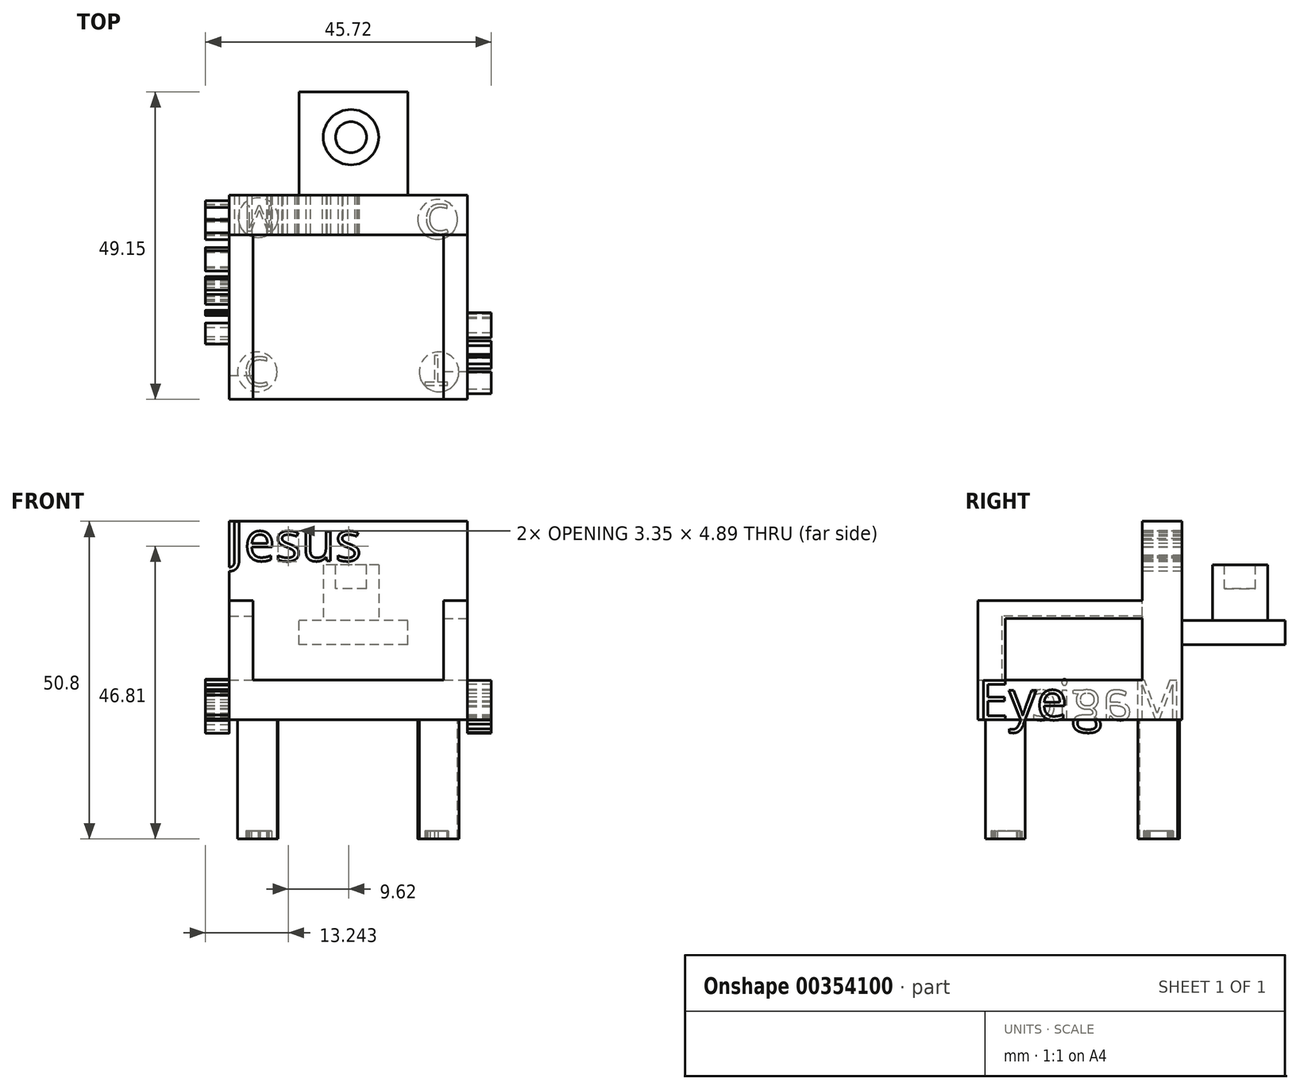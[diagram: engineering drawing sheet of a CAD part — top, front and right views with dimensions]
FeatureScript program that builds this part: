
annotation { "Feature Type Name" : "Feature", "Feature Type Description" : "" }
export const myFeature = defineFeature(function(context is Context, id is Id, definition is map)
    precondition{}
    {
        {
            var Q0;
            Q0=qCreatedBy(makeId("Top.planeOp"),FACE);
            var sketch = newSketch(context, id + "F0", { "sketchPlane" : qUnion([Q0])});
            skLineSegment(sketch, "E0.bottom", {"start": v(-18.82, -4.38) * mm, "end": v(19.28, -4.38) * mm});
            skLineSegment(sketch, "E0.top", {"start": v(-18.82, 28.26) * mm, "end": v(19.28, 28.26) * mm});
            skLineSegment(sketch, "E0.left", {"start": v(-18.82, -4.38) * mm, "end": v(-18.82, 28.26) * mm});
            skLineSegment(sketch, "E0.right", {"start": v(19.28, -4.38) * mm, "end": v(19.28, 28.26) * mm});
            skSolve(sketch);
        }
        {
            var Q0;
            Q0 = qSketchRegion(id + "F0", true);
            extrude(context, id + "F1", {"entities" : qUnion([Q0]), "depth" : 6.35 * mm});
        }
        {
            var Q0;
            Q0=makeQuery(id+"F1.opExtrude","CAP_FACE",FACE,{"disambiguationData":[OSD([sQuery(id+"F0.wireOp",EDGE,"E0.bottom"),sQuery(id+"F0.wireOp",EDGE,"E0.top"),sQuery(id+"F0.wireOp",EDGE,"E0.left"),sQuery(id+"F0.wireOp",EDGE,"E0.right")])],"isStart":false});
            var sketch = newSketch(context, id + "F2", { "sketchPlane" : qUnion([Q0])});
            skLineSegment(sketch, "E1.bottom", {"start": v(-18.82, 21.91) * mm, "end": v(19.28, 21.91) * mm});
            skLineSegment(sketch, "E1.top", {"start": v(-18.82, 28.26) * mm, "end": v(19.28, 28.26) * mm});
            skLineSegment(sketch, "E1.left", {"start": v(-18.82, 21.91) * mm, "end": v(-18.82, 28.26) * mm});
            skLineSegment(sketch, "E1.right", {"start": v(19.28, 21.91) * mm, "end": v(19.28, 28.26) * mm});
            skSolve(sketch);
        }
        {
            var Q0;
            Q0=makeQuery(id+"F2.imprint","IMPRINT",FACE,{"disambiguationData":[TD([[makeQuery(id+"F2.imprint","IMPRINT",EDGE,{"derivedFrom":sQuery(id+"F2.wireOp",EDGE,"E1.bottom")}),1.0]])]});
            extrude(context, id + "F3", {"entities" : qUnion([Q0]), "operationType" : NewBodyOperationType.ADD, "depth" : 25.4 * mm});
        }
        {
            var Q0;
            Q0=makeQuery(id+"F1.opExtrude","CAP_FACE",FACE,{"disambiguationData":[OSD([sQuery(id+"F0.wireOp",EDGE,"E0.bottom"),sQuery(id+"F0.wireOp",EDGE,"E0.top"),sQuery(id+"F0.wireOp",EDGE,"E0.left"),sQuery(id+"F0.wireOp",EDGE,"E0.right")])],"isStart":true});
            var sketch = newSketch(context, id + "F4", { "sketchPlane" : qUnion([Q0])});
            skCircle(sketch, "E2", {"center": v(-14.37, 0) * mm, "radius": 3.18 * mm});
            skSolve(sketch);
        }
        {
            var Q0;
            Q0 = qSketchRegion(id + "F4", true);
            extrude(context, id + "F5", {"entities" : qUnion([Q0]), "operationType" : NewBodyOperationType.ADD, "depth" : 19.05 * mm});
        }
        {
            var Q0;
            Q0=makeQuery(id+"F1.opExtrude","CAP_FACE",FACE,{"disambiguationData":[OSD([sQuery(id+"F0.wireOp",EDGE,"E0.bottom"),sQuery(id+"F0.wireOp",EDGE,"E0.top"),sQuery(id+"F0.wireOp",EDGE,"E0.left"),sQuery(id+"F0.wireOp",EDGE,"E0.right")])],"isStart":true});
            var sketch = newSketch(context, id + "F6", { "sketchPlane" : qUnion([Q0])});
            skCircle(sketch, "E3", {"center": v(14.71, 0) * mm, "radius": 3.18 * mm});
            skSolve(sketch);
        }
        {
            var Q0;
            Q0 = qSketchRegion(id + "F6", true);
            extrude(context, id + "F7", {"entities" : qUnion([Q0]), "operationType" : NewBodyOperationType.ADD, "depth" : 19.05 * mm});
        }
        {
            var Q0;
            Q0=makeQuery(id+"F1.opExtrude","CAP_FACE",FACE,{"disambiguationData":[OSD([sQuery(id+"F0.wireOp",EDGE,"E0.bottom"),sQuery(id+"F0.wireOp",EDGE,"E0.top"),sQuery(id+"F0.wireOp",EDGE,"E0.left"),sQuery(id+"F0.wireOp",EDGE,"E0.right")])],"isStart":true});
            var sketch = newSketch(context, id + "F8", { "sketchPlane" : qUnion([Q0])});
            skCircle(sketch, "E4", {"center": v(-14.23, -24.67) * mm, "radius": 3.18 * mm});
            skSolve(sketch);
        }
        {
            var Q0;
            Q0 = qSketchRegion(id + "F8", true);
            extrude(context, id + "F9", {"entities" : qUnion([Q0]), "operationType" : NewBodyOperationType.ADD, "depth" : 19.05 * mm});
        }
        {
            var Q0;
            Q0=makeQuery(id+"F1.opExtrude","CAP_FACE",FACE,{"disambiguationData":[OSD([sQuery(id+"F0.wireOp",EDGE,"E0.bottom"),sQuery(id+"F0.wireOp",EDGE,"E0.top"),sQuery(id+"F0.wireOp",EDGE,"E0.left"),sQuery(id+"F0.wireOp",EDGE,"E0.right")])],"isStart":true});
            var sketch = newSketch(context, id + "F10", { "sketchPlane" : qUnion([Q0])});
            skCircle(sketch, "E5", {"center": v(14.5, -24.4) * mm, "radius": 3.18 * mm});
            skSolve(sketch);
        }
        {
            var Q0;
            Q0 = qSketchRegion(id + "F10", true);
            extrude(context, id + "F11", {"entities" : qUnion([Q0]), "operationType" : NewBodyOperationType.ADD, "depth" : 19.05 * mm});
        }
        {
            var Q0;
            Q0=makeQuery(id+"F1.opExtrude","CAP_FACE",FACE,{"disambiguationData":[OSD([sQuery(id+"F0.wireOp",EDGE,"E0.bottom"),sQuery(id+"F0.wireOp",EDGE,"E0.top"),sQuery(id+"F0.wireOp",EDGE,"E0.left"),sQuery(id+"F0.wireOp",EDGE,"E0.right")])],"isStart":false});
            var sketch = newSketch(context, id + "F12", { "sketchPlane" : qUnion([Q0])});
            skLineSegment(sketch, "E6.bottom", {"start": v(-18.82, -4.38) * mm, "end": v(-15.01, -4.38) * mm});
            skLineSegment(sketch, "E6.top", {"start": v(-18.82, -0.58) * mm, "end": v(-15.01, -0.58) * mm});
            skLineSegment(sketch, "E6.left", {"start": v(-18.82, -4.38) * mm, "end": v(-18.82, -0.58) * mm});
            skLineSegment(sketch, "E6.right", {"start": v(-15.01, -4.38) * mm, "end": v(-15.01, -0.58) * mm});
            skSolve(sketch);
        }
        {
            var Q0;
            Q0 = qSketchRegion(id + "F12", true);
            extrude(context, id + "F13", {"entities" : qUnion([Q0]), "operationType" : NewBodyOperationType.ADD, "depth" : 12.7 * mm});
        }
        {
            var Q0;
            Q0=makeQuery(id+"F1.opExtrude","CAP_FACE",FACE,{"disambiguationData":[OSD([sQuery(id+"F0.wireOp",EDGE,"E0.bottom"),sQuery(id+"F0.wireOp",EDGE,"E0.top"),sQuery(id+"F0.wireOp",EDGE,"E0.left"),sQuery(id+"F0.wireOp",EDGE,"E0.right")])],"isStart":false});
            var sketch = newSketch(context, id + "F14", { "sketchPlane" : qUnion([Q0])});
            skLineSegment(sketch, "E7.bottom", {"start": v(19.28, -4.38) * mm, "end": v(15.47, -4.38) * mm});
            skLineSegment(sketch, "E7.top", {"start": v(19.28, 0) * mm, "end": v(15.47, 0) * mm});
            skLineSegment(sketch, "E7.left", {"start": v(19.28, -4.38) * mm, "end": v(19.28, 0) * mm});
            skLineSegment(sketch, "E7.right", {"start": v(15.47, -4.38) * mm, "end": v(15.47, 0) * mm});
            skSolve(sketch);
        }
        {
            var Q0;
            Q0 = qSketchRegion(id + "F14", true);
            extrude(context, id + "F15", {"entities" : qUnion([Q0]), "operationType" : NewBodyOperationType.ADD, "depth" : 12.7 * mm});
        }
        {
            var Q0;
            Q0=makeQuery(id+"F13.opExtrude","SWEPT_FACE",FACE,{"disambiguationData":[OSD([sQuery(id+"F12.wireOp",EDGE,"E6.top")])]});
            var sketch = newSketch(context, id + "F16", { "sketchPlane" : qUnion([Q0])});
            skLineSegment(sketch, "E8.bottom", {"start": v(15.01, 16.57) * mm, "end": v(18.82, 16.57) * mm});
            skLineSegment(sketch, "E8.top", {"start": v(15.01, 19.05) * mm, "end": v(18.82, 19.05) * mm});
            skLineSegment(sketch, "E8.left", {"start": v(15.01, 16.57) * mm, "end": v(15.01, 19.05) * mm});
            skLineSegment(sketch, "E8.right", {"start": v(18.82, 16.57) * mm, "end": v(18.82, 19.05) * mm});
            skSolve(sketch);
        }
        {
            var Q0;
            Q0=makeQuery(id+"F16.imprint","IMPRINT",FACE,{"disambiguationData":[TD([[makeQuery(id+"F16.imprint","IMPRINT",EDGE,{"derivedFrom":sQuery(id+"F16.wireOp",EDGE,"E8.bottom")}),1.0]])]});
            extrude(context, id + "F17", {"entities" : qUnion([Q0]), "operationType" : NewBodyOperationType.ADD, "depth" : 25.4 * mm});
        }
        {
            var Q0;
            Q0=makeQuery(id+"F15.opExtrude","SWEPT_FACE",FACE,{"disambiguationData":[OSD([sQuery(id+"F14.wireOp",EDGE,"E7.top")])]});
            var sketch = newSketch(context, id + "F18", { "sketchPlane" : qUnion([Q0])});
            skLineSegment(sketch, "E9.bottom", {"start": v(-19.28, 16.23) * mm, "end": v(-15.47, 16.23) * mm});
            skLineSegment(sketch, "E9.top", {"start": v(-19.28, 19.05) * mm, "end": v(-15.47, 19.05) * mm});
            skLineSegment(sketch, "E9.left", {"start": v(-19.28, 16.23) * mm, "end": v(-19.28, 19.05) * mm});
            skLineSegment(sketch, "E9.right", {"start": v(-15.47, 16.23) * mm, "end": v(-15.47, 19.05) * mm});
            skSolve(sketch);
        }
        {
            var Q0;
            Q0 = qSketchRegion(id + "F18", true);
            extrude(context, id + "F19", {"entities" : qUnion([Q0]), "operationType" : NewBodyOperationType.ADD, "depth" : 25.4 * mm});
        }
        {
            var Q0;
            Q0=makeQuery(id+"F3.opExtrude","SWEPT_FACE",FACE,{"disambiguationData":[OSD([sQuery(id+"F2.wireOp",EDGE,"E1.bottom")])]});
            var sketch = newSketch(context, id + "F20", { "sketchPlane" : qUnion([Q0])});
            skText(sketch, "E10", { "text": "Jesus", "fontName": "OpenSans-Regular.ttf"});
            const initialGuessF20  = {"E10": [-0.01882, 0.0254, 1, 0, 0.00635]};
            skSetInitialGuess(sketch, initialGuessF20);
            skSolve(sketch);
        }
        {
            var Q0;
            Q0 = qSketchRegion(id + "F20", true);
            extrude(context, id + "F21", {"entities" : qUnion([Q0]), "operationType" : NewBodyOperationType.REMOVE, "oppositeDirection" : true, "depth" : 27.28 * mm});
        }
        {
            var Q0;
            {var subQ2=sQuery(id+"F12.wireOp",EDGE,"E6.left");var subQ5=sQuery(id+"F0.wireOp",EDGE,"E0.left");var subQ6=sQuery(id+"F0.wireOp",EDGE,"E0.bottom");Q0=makeQuery(id+"F21.boolean.opBoolean","SPLIT",FACE,{"disambiguationData":[TD([makeQuery(id+"F1.opExtrude","SWEPT_FACE",FACE,{"disambiguationData":[OSD([subQ6])]})])],"derivedFrom":makeQuery(id+"F17.boolean.opBoolean","MERGE",FACE,{"derivedFrom":[makeQuery(id+"F13.boolean.opBoolean","MERGE",FACE,{"derivedFrom":[makeQuery(id+"F3.boolean.opBoolean","MERGE",FACE,{"derivedFrom":[makeQuery(id+"F1.opExtrude","SWEPT_FACE",FACE,{"disambiguationData":[OSD([subQ5])]}),makeQuery(id+"F3.opExtrude","SWEPT_FACE",FACE,{"disambiguationData":[OSD([sQuery(id+"F2.wireOp",EDGE,"E1.left")])]})]}),makeQuery(id+"F13.opExtrude","SWEPT_FACE",FACE,{"disambiguationData":[OSD([subQ2])]})]}),makeQuery(id+"F17.opExtrude","SWEPT_FACE",FACE,{"disambiguationData":[OSD([sQuery(id+"F16.wireOp",EDGE,"E8.right")])]})]})});}
            var sketch = newSketch(context, id + "F22", { "sketchPlane" : qUnion([Q0])});
            skText(sketch, "E11", { "text": "Magic", "fontName": "OpenSans-Regular.ttf"});
            const initialGuessF22  = {"E11": [-0.02826, 0, 1, 0, 0.00635]};
            skSetInitialGuess(sketch, initialGuessF22);
            skSolve(sketch);
        }
        {
            var Q0;
            Q0 = qSketchRegion(id + "F22", true);
            extrude(context, id + "F23", {"entities" : qUnion([Q0]), "operationType" : NewBodyOperationType.ADD, "depth" : 3.8 * mm});
        }
        {
            var Q0;
            Q0=makeQuery(id+"F19.boolean.opBoolean","MERGE",FACE,{"derivedFrom":[makeQuery(id+"F15.boolean.opBoolean","MERGE",FACE,{"derivedFrom":[makeQuery(id+"F3.boolean.opBoolean","MERGE",FACE,{"derivedFrom":[makeQuery(id+"F1.opExtrude","SWEPT_FACE",FACE,{"disambiguationData":[OSD([sQuery(id+"F0.wireOp",EDGE,"E0.right")])]}),makeQuery(id+"F3.opExtrude","SWEPT_FACE",FACE,{"disambiguationData":[OSD([sQuery(id+"F2.wireOp",EDGE,"E1.right")])]})]}),makeQuery(id+"F15.opExtrude","SWEPT_FACE",FACE,{"disambiguationData":[OSD([sQuery(id+"F14.wireOp",EDGE,"E7.left")])]})]}),makeQuery(id+"F19.opExtrude","SWEPT_FACE",FACE,{"disambiguationData":[OSD([sQuery(id+"F18.wireOp",EDGE,"E9.left")])]})]});
            var sketch = newSketch(context, id + "F24", { "sketchPlane" : qUnion([Q0])});
            skText(sketch, "E12", { "text": "Eye", "fontName": "OpenSans-Regular.ttf"});
            const initialGuessF24  = {"E12": [-0.00438, 0, 1, 0, 0.00635]};
            skSetInitialGuess(sketch, initialGuessF24);
            skSolve(sketch);
        }
        {
            var Q0;
            Q0 = qSketchRegion(id + "F24", true);
            extrude(context, id + "F25", {"entities" : qUnion([Q0]), "operationType" : NewBodyOperationType.ADD, "depth" : 3.8 * mm});
        }
        {
            var Q0;
            {var subQ2=sQuery(id+"F2.wireOp",EDGE,"E1.top");var subQ4=sQuery(id+"F0.wireOp",EDGE,"E0.left");var subQ5=sQuery(id+"F0.wireOp",EDGE,"E0.top");Q0=makeQuery(id+"F21.boolean.opBoolean","SPLIT",FACE,{"disambiguationData":[TD([makeQuery(id+"F1.opExtrude","SWEPT_FACE",FACE,{"disambiguationData":[OSD([subQ4])]})])],"derivedFrom":makeQuery(id+"F3.boolean.opBoolean","MERGE",FACE,{"derivedFrom":[makeQuery(id+"F1.opExtrude","SWEPT_FACE",FACE,{"disambiguationData":[OSD([subQ5])]}),makeQuery(id+"F3.opExtrude","SWEPT_FACE",FACE,{"disambiguationData":[OSD([subQ2])]})]})});}
            var sketch = newSketch(context, id + "F26", { "sketchPlane" : qUnion([Q0])});
            skPoint(sketch, "E13.oppositeSnap0", {"position": v(-19.28, 15.87) * mm});
            skLineSegment(sketch, "E13.bottom", {"start": v(-9.7, 12) * mm, "end": v(7.66, 12) * mm});
            skLineSegment(sketch, "E13.top", {"start": v(-9.7, 15.87) * mm, "end": v(7.66, 15.87) * mm});
            skLineSegment(sketch, "E13.left", {"start": v(-9.7, 12) * mm, "end": v(-9.7, 15.87) * mm});
            skLineSegment(sketch, "E13.right", {"start": v(7.66, 12) * mm, "end": v(7.66, 15.87) * mm});
            skSolve(sketch);
        }
        {
            var Q0;
            Q0 = qSketchRegion(id + "F26", true);
            extrude(context, id + "F27", {"entities" : qUnion([Q0]), "operationType" : NewBodyOperationType.ADD, "depth" : 16.5 * mm});
        }
        {
            var Q0;
            Q0=makeQuery(id+"F27.opExtrude","SWEPT_FACE",FACE,{"disambiguationData":[OSD([sQuery(id+"F26.wireOp",EDGE,"E13.top")])]});
            var sketch = newSketch(context, id + "F28", { "sketchPlane" : qUnion([Q0])});
            skCircle(sketch, "E14", {"center": v(0.63, 37.54) * mm, "radius": 4.43 * mm});
            skSolve(sketch);
        }
        {
            var Q0;
            Q0 = qSketchRegion(id + "F28", true);
            extrude(context, id + "F29", {"entities" : qUnion([Q0]), "operationType" : NewBodyOperationType.ADD, "depth" : 8.9 * mm});
        }
        {
            var Q0;
            Q0=makeQuery(id+"F29.opExtrude","CAP_FACE",FACE,{"disambiguationData":[OSD([sQuery(id+"F28.wireOp",EDGE,"E14")])],"isStart":false});
            var sketch = newSketch(context, id + "F30", { "sketchPlane" : qUnion([Q0])});
            skCircle(sketch, "E15", {"center": v(0.63, 37.54) * mm, "radius": 2.48 * mm});
            skSolve(sketch);
        }
        {
            var Q0;
            Q0 = qSketchRegion(id + "F30", true);
            extrude(context, id + "F31", {"entities" : qUnion([Q0]), "operationType" : NewBodyOperationType.REMOVE, "oppositeDirection" : true, "depth" : 3.8 * mm});
        }
        {
            var Q0;
            Q0=makeQuery(id+"F9.opExtrude","CAP_FACE",FACE,{"disambiguationData":[OSD([sQuery(id+"F8.wireOp",EDGE,"E4")])],"isStart":false});
            var sketch = newSketch(context, id + "F32", { "sketchPlane" : qUnion([Q0])});
            skText(sketch, "E16", { "text": "M", "fontName": "OpenSans-Regular.ttf"});
            const initialGuessF32  = {"E16": [-0.01657, -0.02657, 1, 0, 0.00404]};
            skSetInitialGuess(sketch, initialGuessF32);
            skSolve(sketch);
        }
        {
            var Q0;
            Q0 = qSketchRegion(id + "F32", true);
            extrude(context, id + "F33", {"entities" : qUnion([Q0]), "operationType" : NewBodyOperationType.REMOVE, "oppositeDirection" : true, "depth" : 1.27 * mm});
        }
        {
            var Q0;
            Q0=makeQuery(id+"F5.opExtrude","CAP_FACE",FACE,{"disambiguationData":[OSD([sQuery(id+"F4.wireOp",EDGE,"E2")])],"isStart":false});
            var sketch = newSketch(context, id + "F34", { "sketchPlane" : qUnion([Q0])});
            skText(sketch, "E17", { "text": "C", "fontName": "OpenSans-Regular.ttf"});
            const initialGuessF34  = {"E17": [-0.01655, -0.00236, 1, 0, 0.00466]};
            skSetInitialGuess(sketch, initialGuessF34);
            skSolve(sketch);
        }
        {
            var Q0;
            Q0 = qSketchRegion(id + "F34", true);
            extrude(context, id + "F35", {"entities" : qUnion([Q0]), "operationType" : NewBodyOperationType.REMOVE, "oppositeDirection" : true, "depth" : 1.27 * mm});
        }
        {
            var Q0;
            Q0=makeQuery(id+"F11.opExtrude","CAP_FACE",FACE,{"disambiguationData":[OSD([sQuery(id+"F10.wireOp",EDGE,"E5")])],"isStart":false});
            var sketch = newSketch(context, id + "F36", { "sketchPlane" : qUnion([Q0])});
            skText(sketch, "E18", { "text": "C", "fontName": "OpenSans-Regular.ttf"});
            const initialGuessF36  = {"E18": [0.0123, -0.02675, 1, 0, 0.00466]};
            skSetInitialGuess(sketch, initialGuessF36);
            skSolve(sketch);
        }
        {
            var Q0;
            Q0 = qSketchRegion(id + "F36", true);
            extrude(context, id + "F37", {"entities" : qUnion([Q0]), "operationType" : NewBodyOperationType.REMOVE, "oppositeDirection" : true, "depth" : 1.27 * mm});
        }
        {
            var Q0;
            Q0=makeQuery(id+"F7.opExtrude","CAP_FACE",FACE,{"disambiguationData":[OSD([sQuery(id+"F6.wireOp",EDGE,"E3")])],"isStart":false});
            var sketch = newSketch(context, id + "F38", { "sketchPlane" : qUnion([Q0])});
            skText(sketch, "E19", { "text": "T", "fontName": "OpenSans-Regular.ttf"});
            const initialGuessF38  = {"E19": [0.01241, -0.00263, 1, 0, 0.00482]};
            skSetInitialGuess(sketch, initialGuessF38);
            skSolve(sketch);
        }
        {
            var Q0;
            Q0 = qSketchRegion(id + "F38", true);
            extrude(context, id + "F39", {"entities" : qUnion([Q0]), "operationType" : NewBodyOperationType.REMOVE, "oppositeDirection" : true, "depth" : 1.27 * mm});
        }
    });
